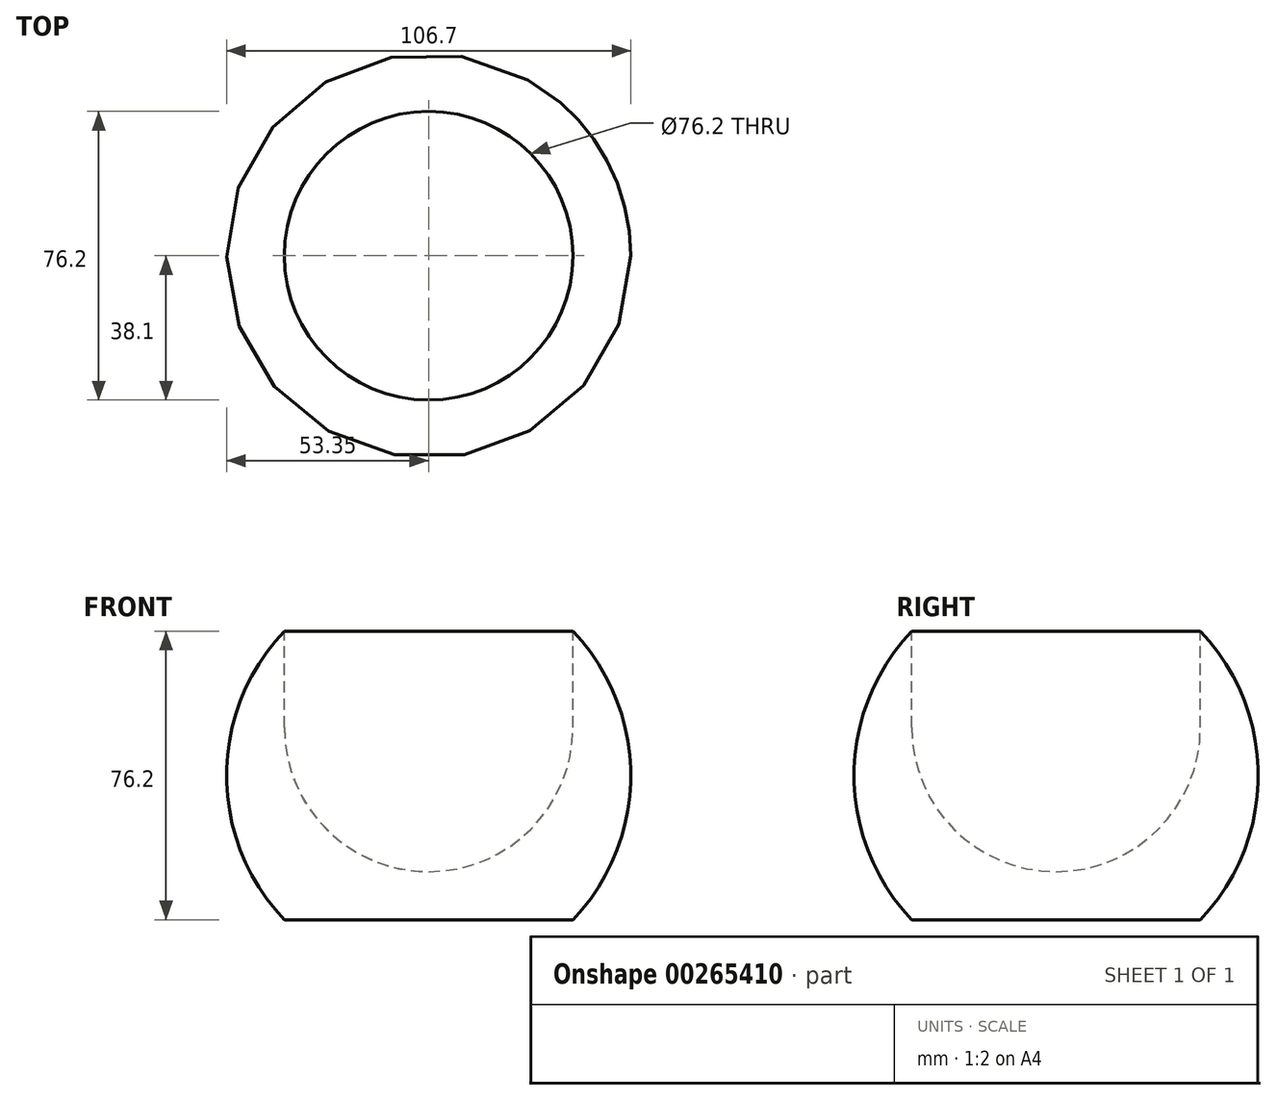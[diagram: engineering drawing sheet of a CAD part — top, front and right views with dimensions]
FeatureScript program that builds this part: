
annotation { "Feature Type Name" : "Feature", "Feature Type Description" : "" }
export const myFeature = defineFeature(function(context is Context, id is Id, definition is map)
    precondition{}
    {
        {
            var Q0;
            Q0=qCreatedBy(makeId("Front.planeOp"),FACE);
            var sketch = newSketch(context, id + "F0", { "sketchPlane" : qUnion([Q0])});
            skLineSegment(sketch, "E0.bottom", {"start": v(38.1, -38.1) * mm, "end": v(0, -38.1) * mm});
            skLineSegment(sketch, "E0.top", {"start": v(38.1, 38.1) * mm, "end": v(0, 38.1) * mm});
            skPoint(sketch, "E0.middle", {"position": v(0, 0) * mm});
            skLineSegment(sketch, "E1", {"start": v(0, 38.1) * mm, "end": v(0, -38.1) * mm});
            skPoint(sketch, "E2.orphan", {"position": v(-38.1, 38.1) * mm});
            skPoint(sketch, "E3.orphan", {"position": v(-38.1, -38.1) * mm});
            skArc(sketch, "E4", {"start": v(38.1, -38.1) * mm, "mid": v(53.35, 0) * mm, "end": v(38.1, 38.1) * mm});
            skSolve(sketch);
        }
        {
            var Q0;
            Q0=makeQuery(id+"F0.imprint","IMPRINT",FACE,{"disambiguationData":[TD([[makeQuery(id+"F0.imprint","IMPRINT",EDGE,{"derivedFrom":sQuery(id+"F0.wireOp",EDGE,"E0.bottom")}),-1.0]])]});
            var Q1;
            Q1=sQuery(id+"F0.wireOp",EDGE,"E1");
            revolve(context, id + "F1", {"entities" : qUnion([Q0]), "axis" : qUnion([Q1]), "revolveType" : RevolveType.FULL});
        }
        {
            var Q0;
            Q0=makeQuery(id+"F1.opRevolve","SWEPT_FACE",FACE,{"disambiguationData":[OSD([sQuery(id+"F0.wireOp",EDGE,"E0.top")])]});
            extrude(context, id + "F2", {"entities" : qUnion([Q0]), "operationType" : NewBodyOperationType.REMOVE, "oppositeDirection" : true, "depth" : 63.5 * mm});
        }
        {
            var Q0;
            Q0=makeQuery(id+"F2.boolean.opBoolean","COPY",EDGE,{"derivedFrom":makeQuery(id+"F2.opExtrude","CAP_EDGE",EDGE,{"disambiguationData":[OSD([sQuery(id+"F0.wireOp",EDGE,"E0.top"),sQuery(id+"F0.wireOp",EDGE,"E4")])],"isStart":false})});
            fillet(context, id + "F3", {"entities" : qUnion([Q0]), "radius" : 38.1 * mm, "tangentPropagation" : true, "allowEdgeOverflow" : false});
        }
    });
